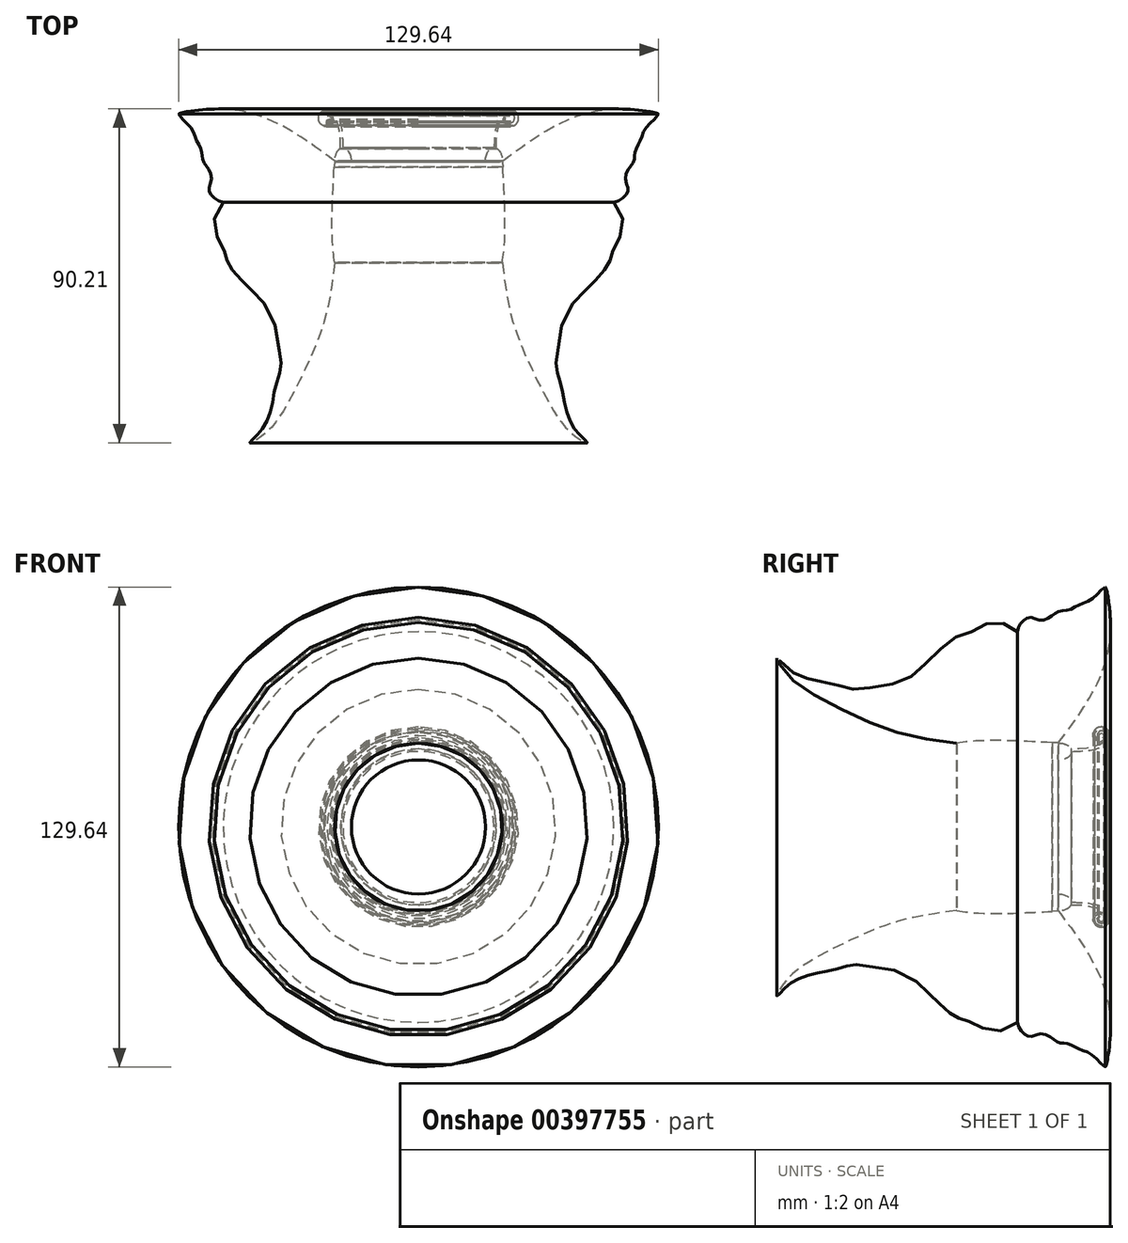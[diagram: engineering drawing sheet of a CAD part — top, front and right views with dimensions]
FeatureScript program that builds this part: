
annotation { "Feature Type Name" : "Feature", "Feature Type Description" : "" }
export const myFeature = defineFeature(function(context is Context, id is Id, definition is map)
    precondition{}
    {
        {
            var Q0;
            Q0=qCreatedBy(makeId("Top.planeOp"),FACE);
            var sketch = newSketch(context, id + "F0", { "sketchPlane" : qUnion([Q0])});
            skEllipticalArc(sketch, "E0", {});
            skEllipticalArc(sketch, "E1", {});
            skFitSpline(sketch, "E2", {"points": [v(2.3, 20.9) * mm, v(2.89, 0) * mm, v(1.74, -9.47) * mm], "startDerivative": vector(2.01, -38.53) * mm, "endDerivative": vector(-3.6, -21.18) * mm});
            skFitSpline(sketch, "E3", {"points": [v(-2.3, 20.9) * mm, v(-3.05, 0) * mm, v(-1.74, -9.47) * mm], "startDerivative": vector(-2.5, -38.54) * mm, "endDerivative": vector(4.14, -21.16) * mm});
            skEllipticalArc(sketch, "E4", {});
            skFitSpline(sketch, "E5", {"points": [v(-2.3, 20.9) * mm, v(0, 20.9) * mm, v(2.3, 20.9) * mm], "startDerivative": vector(4.7, -2.5) * mm, "endDerivative": vector(4.7, 2.5) * mm});
            skFitSpline(sketch, "E6", {"points": [v(-2.4, 19.25) * mm, v(0, 18.83) * mm, v(2.38, 19.24) * mm], "startDerivative": vector(4.9, -2.33) * mm, "endDerivative": vector(4.87, 2.3) * mm});
            skFitSpline(sketch, "E7", {"points": [v(2.3, 20.9) * mm, v(15.85, 30.1) * mm, v(32.92, 34.98) * mm, v(44.41, 33.58) * mm, v(36.58, 33.58) * mm, v(28.57, 33.06) * mm, v(16.1, 28.61) * mm, v(2.38, 19.24) * mm], "startDerivative": vector(81.12, 61.53) * mm, "endDerivative": vector(-77.6, -62.7) * mm});
            skFitSpline(sketch, "E8", {"points": [v(2.38, 19.24) * mm, v(12.47, 14.95) * mm, v(28.81, 10.34) * mm, v(32.38, 9.81) * mm, v(34.78, 10.9) * mm, v(36.24, 13.24) * mm, v(35.51, 15.87) * mm, v(36.39, 18.85) * mm, v(37.78, 20.9) * mm, v(38.21, 23.65) * mm, v(39.54, 26.37) * mm, v(41.1, 29.93) * mm, v(44.41, 33.58) * mm], "startDerivative": vector(70.32, -29.03) * mm, "endDerivative": vector(18.2, 40.24) * mm});
            skFitSpline(sketch, "E9", {"points": [v(2.22, -6.62) * mm, v(4.74, -21.24) * mm, v(9.72, -34.27) * mm, v(16.75, -47.59) * mm, v(22.16, -53.59) * mm, v(25.24, -55.2) * mm, v(22.5, -52.37) * mm, v(20.7, -49.53) * mm, v(19.34, -45.75) * mm, v(18.72, -42.23) * mm, v(17.47, -37.47) * mm, v(16.77, -34.04) * mm, v(17.42, -29.11) * mm, v(19.07, -20.9) * mm, v(22.35, -16.46) * mm, v(27.45, -11.2) * mm, v(31.06, -6.62) * mm, v(32.38, -2.5) * mm, v(34.51, 1.61) * mm, v(34.51, 6.21) * mm, v(32.38, 9.81) * mm], "startDerivative": vector(24.83, -191.18) * mm, "endDerivative": vector(-60.54, 80.48) * mm});
            skEllipse(sketch, "E10", {"center": v(28.24, 24.96) * mm, "majorRadius": 3.27 * mm, "minorRadius": 1.36 * mm, "majorAxis": v(0.84, 0.54)});
            skEllipse(sketch, "E11", {"center": v(28.24, 24.96) * mm, "majorRadius": 1.8 * mm, "minorRadius": 0.84 * mm, "majorAxis": v(0.82, 0.57)});
            skEllipse(sketch, "E12", {"center": v(24.15, 5.65) * mm, "majorRadius": 2.9 * mm, "minorRadius": 1.52 * mm, "majorAxis": v(0.82, -0.57)});
            skEllipse(sketch, "E13", {"center": v(24.15, 5.65) * mm, "majorRadius": 2.05 * mm, "minorRadius": 0.86 * mm, "majorAxis": v(0.76, -0.65)});
            skFitSpline(sketch, "E14", {"points": [v(2.22, -6.62) * mm, v(2.22, -6.56) * mm], "startDerivative": vector(0, 0.06) * mm, "endDerivative": vector(0, 0.06) * mm});
            skLineSegment(sketch, "E15", {"start": v(2.22, -6.56) * mm, "end": v(2.22, -6.55) * mm});
            skArc(sketch, "E16", {"start": v(3.2, 30.63) * mm, "mid": v(6.58, 31.93) * mm, "end": v(4.26, 34.7) * mm});
            skFitSpline(sketch, "E17", {"points": [v(0, 24.44) * mm, v(0.17, 27.52) * mm, v(0.46, 30.02) * mm, v(1.38, 32.67) * mm, v(2.86, 34.16) * mm, v(4.26, 34.7) * mm, v(5.9, 34.15) * mm, v(6.54, 33.17) * mm, v(6.42, 31.5) * mm, v(5.17, 30.4) * mm, v(3.2, 30.63) * mm, v(2.58, 32.37) * mm, v(3.43, 33.46) * mm, v(4.47, 33.63) * mm, v(5.32, 33.33) * mm, v(5.54, 32.83) * mm, v(5.46, 31.98) * mm, v(5, 31.43) * mm, v(4.06, 31.54) * mm, v(3.73, 32.07) * mm, v(4.64, 31.8) * mm, v(5.1, 32.7) * mm, v(4.5, 33.16) * mm, v(3.6, 33) * mm, v(3.02, 32.23) * mm, v(3.46, 31.08) * mm, v(5.02, 30.75) * mm, v(6.02, 31.63) * mm, v(6.13, 33.11) * mm, v(5.5, 33.9) * mm, v(4.27, 34.21) * mm, v(3.05, 33.74) * mm, v(1.87, 32.34) * mm, v(1.14, 29.93) * mm, v(0.72, 27.44) * mm, v(0.67, 24.28) * mm], "startDerivative": vector(3.76, 75.56) * mm, "endDerivative": vector(0.96, -77.04) * mm});
            skFitSpline(sketch, "E18", {"points": [v(2.38, 19.24) * mm, v(6.91, 21.58) * mm, v(16.42, 27.5) * mm, v(28.7, 31.98) * mm, v(36.58, 32.61) * mm, v(43.66, 33.11) * mm, v(36.58, 31.98) * mm, v(28.73, 31.35) * mm, v(16.53, 26.57) * mm, v(7.08, 21.11) * mm, v(2.38, 19.24) * mm]});
            skFitSpline(sketch, "E19", {"points": [v(3.89, 16) * mm, v(8, 13.7) * mm, v(12.47, 11.56) * mm, v(16.7, 10.04) * mm, v(24.01, 8.77) * mm, v(20.07, 8.11) * mm, v(20.15, 5.49) * mm, v(23.1, 2.28) * mm, v(26.97, 1.63) * mm, v(29.1, 2.7) * mm, v(27.05, 0.15) * mm, v(22.12, 1.05) * mm, v(18.5, 4.91) * mm, v(17.52, 7.43) * mm, v(12.47, 9.76) * mm, v(7.59, 12.3) * mm, v(3.89, 16) * mm]});
            skFitSpline(sketch, "E20", {"points": [v(5.46, 9.78) * mm, v(10.98, 6.1) * mm, v(15.51, 2.9) * mm, v(19.7, -3.33) * mm, v(18.04, -7.97) * mm, v(12.47, -7.2) * mm, v(12.47, -2.77) * mm, v(15.68, -3.9) * mm, v(13.83, -5.32) * mm, v(17.46, -5.96) * mm, v(17.35, -3.33) * mm, v(14.6, 0) * mm, v(9.86, 0) * mm, v(8.99, -8.85) * mm, v(10.9, -14.68) * mm, v(14.72, -14.4) * mm, v(16.47, -12.87) * mm, v(12.47, -19.72) * mm, v(12.04, -24.36) * mm, v(10.55, -27.84) * mm, v(8.92, -21.48) * mm, v(8.26, -16.46) * mm, v(7.13, -8.6) * mm, v(6.38, 0) * mm, v(6.08, 2.9) * mm, v(5.85, 7.32) * mm, v(5.46, 9.78) * mm]});
            skPoint(sketch, "E21.6.internal.snap0", {"position": v(27.52, 26.1) * mm});
            skFitSpline(sketch, "E21", {"points": [v(7.6, 19.77) * mm, v(15.95, 23.96) * mm, v(21.25, 26.36) * mm, v(24.34, 28.44) * mm, v(23.14, 24.47) * mm, v(23.41, 22.07) * mm, v(27.52, 21.38) * mm, v(29.13, 21.66) * mm, v(27.1, 19.54) * mm, v(23.04, 18.8) * mm, v(17.7, 18.9) * mm, v(12.3, 19.08) * mm, v(7.6, 19.77) * mm]});
            skFitSpline(sketch, "E22.MirrorCS", {"points": [v(-2.22, -6.62) * mm, v(-2.22, -6.56) * mm], "startDerivative": vector(0, 0.06) * mm, "endDerivative": vector(0, 0.06) * mm});
            skLineSegment(sketch, "E23.MirrorCS", {"start": v(-2.22, -6.56) * mm, "end": v(-2.22, -6.55) * mm});
            skEllipticalArc(sketch, "E24.MirrorCS", {});
            skEllipticalArc(sketch, "E25.MirrorCS", {});
            skFitSpline(sketch, "E26.MirrorCS", {"points": [v(2.3, 20.9) * mm, v(0, 20.9) * mm, v(-2.3, 20.9) * mm], "startDerivative": vector(-4.7, -2.5) * mm, "endDerivative": vector(-4.7, 2.5) * mm});
            skFitSpline(sketch, "E27.MirrorCS", {"points": [v(2.4, 19.25) * mm, v(0, 18.83) * mm, v(-2.38, 19.24) * mm], "startDerivative": vector(-4.9, -2.33) * mm, "endDerivative": vector(-4.87, 2.3) * mm});
            skEllipticalArc(sketch, "E28.MirrorCS", {});
            skLineSegment(sketch, "E29", {"start": v(-20.4, 52.86) * mm, "end": v(-20.4, -60.76) * mm});
            skPoint(sketch, "E30.orphan", {"position": v(0, 43.1) * mm});
            const initialGuessF0  = {"E0": [0, 0.02090463444890858, 0, -1, 0.0035310519394098046, 0.002297039903684678, 1.5707963267948966, 4.71238898038469], "E1": [0, -0.009469367382299913, 0, 1, 0.0035901373358472096, 0.001739675895624183, 1.5707963267948966, 4.71238898038469], "E4": [0.001387894892873516, 0.023718264862181527, 0.3162766123089874, -0.9486670145558718, 0.0018780809074936957, 0.0005518705882354958, 4.293777265012078, 0.42567047345905185], "E24.MirrorCS": [0, 0.02090463444890858, 0, -1, 0.0035310519394098046, 0.002297039903684678, 1.5707963267948966, 4.71238898038469], "E25.MirrorCS": [-0.001387894892873516, 0.023718264862181527, -0.3162766123089874, -0.9486670145558718, 0.0018780809074936957, 0.0005518705882354958, 5.8575148337205345, 1.9894080421675087], "E28.MirrorCS": [0, -0.009469367382299913, 0, 1, 0.0035901373358472096, 0.001739675895624183, 1.5707963267948966, 4.71238898038469]};
            skSetInitialGuess(sketch, initialGuessF0);
            skSolve(sketch);
        }
        {
            var Q0;
            Q0=makeQuery(id+"F0.imprint","IMPRINT",FACE,{"disambiguationData":[TD([[makeQuery(id+"F0.imprint","IMPRINT",EDGE,{"derivedFrom":sQuery(id+"F0.wireOp",EDGE,"E10")}),-1.0]])]});
            var Q1;
            Q1=makeQuery(id+"F0.imprint","IMPRINT",FACE,{"disambiguationData":[TD([[makeQuery(id+"F0.imprint","IMPRINT",EDGE,{"derivedFrom":sQuery(id+"F0.wireOp",EDGE,"E20")}),-1.0]])]});
            var Q2;
            Q2=makeQuery(id+"F0.imprint","IMPRINT",FACE,{"disambiguationData":[TD([[makeQuery(id+"F0.imprint","IMPRINT",EDGE,{"derivedFrom":sQuery(id+"F0.wireOp",EDGE,"E21")}),-1.0]])]});
            var Q3;
            {var subQ0=sQuery(id+"F0.wireOp",EDGE,"E9");Q3=makeQuery(id+"F0.imprint","IMPRINT",FACE,{"disambiguationData":[TD([[makeQuery(id+"F0.imprint","IMPRINT",EDGE,{"derivedFrom":subQ0}),1.0]])]});}
            var Q4;
            {var subQ1=sQuery(id+"F0.wireOp",EDGE,"E7");var subQ5=makeQuery(id+"F0.imprint","INTERSECT",VERTEX,{"derivedFrom":[subQ1,sQuery(id+"F0.wireOp",EDGE,"E8")]});Q4=makeQuery(id+"F0.imprint","IMPRINT",FACE,{"disambiguationData":[TD([[makeQuery(id+"F0.imprint","IMPRINT",EDGE,{"disambiguationData":[TD([[subQ5,-1.0]])],"derivedFrom":subQ1}),-1.0]])]});}
            var Q5;
            {var subQ0=sQuery(id+"F0.wireOp",EDGE,"E28.MirrorCS");Q5=makeQuery(id+"F0.imprint","IMPRINT",FACE,{"disambiguationData":[TD([[makeQuery(id+"F0.imprint","IMPRINT",EDGE,{"derivedFrom":subQ0}),1.0]])]});}
            var Q6;
            Q6=makeQuery(id+"F0.imprint","IMPRINT",FACE,{"disambiguationData":[TD([[makeQuery(id+"F0.imprint","IMPRINT",EDGE,{"derivedFrom":sQuery(id+"F0.wireOp",EDGE,"E10")}),1.0]])]});
            var Q7;
            Q7=makeQuery(id+"F0.imprint","IMPRINT",FACE,{"disambiguationData":[TD([[makeQuery(id+"F0.imprint","IMPRINT",EDGE,{"derivedFrom":sQuery(id+"F0.wireOp",EDGE,"E12")}),1.0]])]});
            var Q8;
            Q8=makeQuery(id+"F0.imprint","IMPRINT",FACE,{"disambiguationData":[TD([[makeQuery(id+"F0.imprint","IMPRINT",EDGE,{"derivedFrom":sQuery(id+"F0.wireOp",EDGE,"E19")}),-1.0]])]});
            var Q9;
            {var subQ0=sQuery(id+"F0.wireOp",EDGE,"E7");var subQ1=makeQuery(id+"F0.imprint","INTERSECT",VERTEX,{"derivedFrom":[subQ0,sQuery(id+"F0.wireOp",EDGE,"E27.MirrorCS")]});Q9=makeQuery(id+"F0.imprint","IMPRINT",FACE,{"disambiguationData":[TD([[makeQuery(id+"F0.imprint","IMPRINT",EDGE,{"disambiguationData":[TD([[subQ1,1.0]])],"derivedFrom":subQ0}),1.0]])]});}
            var Q10;
            {var subQ0=sQuery(id+"F0.wireOp",EDGE,"E17");var subQ1=sQuery(id+"F0.wireOp",EDGE,"E16");var subQ10=makeQuery(id+"F0.imprint","INTERSECT",VERTEX,{"disambiguationData":[OD(0.0)],"derivedFrom":[subQ1,subQ0]});Q10=makeQuery(id+"F0.imprint","IMPRINT",FACE,{"disambiguationData":[TD([[makeQuery(id+"F0.imprint","IMPRINT",EDGE,{"disambiguationData":[TD([[subQ10,-1.0]])],"derivedFrom":subQ1}),1.0]])]});}
            var Q11;
            Q11=makeQuery(id+"F0.imprint","IMPRINT",FACE,{"disambiguationData":[TD([[makeQuery(id+"F0.imprint","IMPRINT",EDGE,{"derivedFrom":sQuery(id+"F0.wireOp",EDGE,"E13")}),1.0]])]});
            var Q12;
            Q12=makeQuery(id+"F0.imprint","IMPRINT",FACE,{"disambiguationData":[TD([[makeQuery(id+"F0.imprint","IMPRINT",EDGE,{"derivedFrom":sQuery(id+"F0.wireOp",EDGE,"E11")}),1.0]])]});
            var Q13;
            {var subQ0=sQuery(id+"F0.wireOp",EDGE,"E17");var subQ1=sQuery(id+"F0.wireOp",EDGE,"E16");var subQ2=makeQuery(id+"F0.imprint","INTERSECT",VERTEX,{"disambiguationData":[OD(0.0)],"derivedFrom":[subQ1,subQ0]});Q13=makeQuery(id+"F0.imprint","IMPRINT",FACE,{"disambiguationData":[TD([[makeQuery(id+"F0.imprint","IMPRINT",EDGE,{"disambiguationData":[TD([[subQ2,-1.0]])],"derivedFrom":subQ1}),-1.0]])]});}
            var Q14;
            {var subQ0=sQuery(id+"F0.wireOp",EDGE,"E17");var subQ1=sQuery(id+"F0.wireOp",EDGE,"E16");var subQ2=makeQuery(id+"F0.imprint","INTERSECT",VERTEX,{"disambiguationData":[OD(2.0)],"derivedFrom":[subQ1,subQ0]});Q14=makeQuery(id+"F0.imprint","IMPRINT",FACE,{"disambiguationData":[TD([[makeQuery(id+"F0.imprint","IMPRINT",EDGE,{"disambiguationData":[TD([[subQ2,-1.0]])],"derivedFrom":subQ1}),1.0]])]});}
            var Q15;
            {var subQ0=sQuery(id+"F0.wireOp",EDGE,"E17");var subQ1=sQuery(id+"F0.wireOp",EDGE,"E16");var subQ2=makeQuery(id+"F0.imprint","INTERSECT",VERTEX,{"disambiguationData":[OD(3.0)],"derivedFrom":[subQ1,subQ0]});Q15=makeQuery(id+"F0.imprint","IMPRINT",FACE,{"disambiguationData":[TD([[makeQuery(id+"F0.imprint","IMPRINT",EDGE,{"disambiguationData":[TD([[subQ2,-1.0]])],"derivedFrom":subQ1}),-1.0]])]});}
            var Q16;
            {var subQ0=sQuery(id+"F0.wireOp",EDGE,"E17");var subQ1=sQuery(id+"F0.wireOp",EDGE,"E16");var subQ2=makeQuery(id+"F0.imprint","INTERSECT",VERTEX,{"disambiguationData":[OD(4.0)],"derivedFrom":[subQ1,subQ0]});Q16=makeQuery(id+"F0.imprint","IMPRINT",FACE,{"disambiguationData":[TD([[makeQuery(id+"F0.imprint","IMPRINT",EDGE,{"disambiguationData":[TD([[subQ2,-1.0]])],"derivedFrom":subQ1}),1.0]])]});}
            var Q17;
            {var subQ0=sQuery(id+"F0.wireOp",EDGE,"E17");var subQ1=sQuery(id+"F0.wireOp",EDGE,"E16");var subQ2=makeQuery(id+"F0.imprint","INTERSECT",VERTEX,{"disambiguationData":[OD(5.0)],"derivedFrom":[subQ1,subQ0]});Q17=makeQuery(id+"F0.imprint","IMPRINT",FACE,{"disambiguationData":[TD([[makeQuery(id+"F0.imprint","IMPRINT",EDGE,{"disambiguationData":[TD([[subQ2,-1.0]])],"derivedFrom":subQ1}),-1.0]])]});}
            var Q18;
            {var subQ0=sQuery(id+"F0.wireOp",EDGE,"E17");var subQ1=sQuery(id+"F0.wireOp",EDGE,"E16");var subQ2=makeQuery(id+"F0.imprint","INTERSECT",VERTEX,{"disambiguationData":[OD(1.0)],"derivedFrom":[subQ1,subQ0]});Q18=makeQuery(id+"F0.imprint","IMPRINT",FACE,{"disambiguationData":[TD([[makeQuery(id+"F0.imprint","IMPRINT",EDGE,{"disambiguationData":[TD([[subQ2,1.0]])],"derivedFrom":subQ1}),1.0]])]});}
            var Q19;
            {var subQ0=sQuery(id+"F0.wireOp",EDGE,"E4");Q19=makeQuery(id+"F0.imprint","IMPRINT",FACE,{"disambiguationData":[TD([[makeQuery(id+"F0.imprint","IMPRINT",EDGE,{"derivedFrom":subQ0}),1.0]])]});}
            var Q20;
            {var subQ0=sQuery(id+"F0.wireOp",EDGE,"E25.MirrorCS");Q20=makeQuery(id+"F0.imprint","IMPRINT",FACE,{"disambiguationData":[TD([[makeQuery(id+"F0.imprint","IMPRINT",EDGE,{"derivedFrom":subQ0}),1.0]])]});}
            var Q21;
            {var subQ5=sQuery(id+"F0.wireOp",EDGE,"E4");Q21=makeQuery(id+"F0.imprint","IMPRINT",FACE,{"disambiguationData":[TD([[makeQuery(id+"F0.imprint","IMPRINT",EDGE,{"derivedFrom":subQ5}),-1.0]])]});}
            var Q22;
            {var subQ0=sQuery(id+"F0.wireOp",EDGE,"E26.MirrorCS");Q22=makeQuery(id+"F0.imprint","IMPRINT",FACE,{"disambiguationData":[TD([[makeQuery(id+"F0.imprint","IMPRINT",EDGE,{"derivedFrom":subQ0}),1.0]])]});}
            var Q23;
            {var subQ0=sQuery(id+"F0.wireOp",EDGE,"E27.MirrorCS");var subQ1=sQuery(id+"F0.wireOp",EDGE,"E2");var subQ2=makeQuery(id+"F0.imprint","INTERSECT",VERTEX,{"derivedFrom":[subQ1,subQ0]});Q23=makeQuery(id+"F0.imprint","IMPRINT",FACE,{"disambiguationData":[TD([[makeQuery(id+"F0.imprint","IMPRINT",EDGE,{"disambiguationData":[TD([[subQ2,-1.0]])],"derivedFrom":subQ1}),-1.0]])]});}
            var Q24;
            {var subQ0=sQuery(id+"F0.wireOp",EDGE,"E27.MirrorCS");var subQ1=sQuery(id+"F0.wireOp",EDGE,"E7");var subQ2=makeQuery(id+"F0.imprint","INTERSECT",VERTEX,{"derivedFrom":[subQ1,subQ0]});Q24=makeQuery(id+"F0.imprint","IMPRINT",FACE,{"disambiguationData":[TD([[makeQuery(id+"F0.imprint","IMPRINT",EDGE,{"disambiguationData":[TD([[subQ2,1.0]])],"derivedFrom":subQ1}),-1.0]])]});}
            var Q25;
            {var subQ0=sQuery(id+"F0.wireOp",EDGE,"E18");var subQ1=sQuery(id+"F0.wireOp",EDGE,"E2");var subQ3=makeQuery(id+"F0.imprint","INTERSECT",VERTEX,{"derivedFrom":[subQ1,subQ0]});Q25=makeQuery(id+"F0.imprint","IMPRINT",FACE,{"disambiguationData":[TD([[makeQuery(id+"F0.imprint","IMPRINT",EDGE,{"disambiguationData":[TD([[subQ3,-1.0]])],"derivedFrom":subQ1}),-1.0]])]});}
            var Q26;
            {var subQ0=sQuery(id+"F0.wireOp",EDGE,"E18");var subQ1=sQuery(id+"F0.wireOp",EDGE,"E8");var subQ3=makeQuery(id+"F0.imprint","INTERSECT",VERTEX,{"derivedFrom":[subQ1,subQ0]});Q26=makeQuery(id+"F0.imprint","IMPRINT",FACE,{"disambiguationData":[TD([[makeQuery(id+"F0.imprint","IMPRINT",EDGE,{"disambiguationData":[TD([[subQ3,1.0]])],"derivedFrom":subQ1}),-1.0]])]});}
            var Q27;
            {var subQ0=sQuery(id+"F0.wireOp",EDGE,"E18");var subQ2=sQuery(id+"F0.wireOp",EDGE,"E2");var subQ4=makeQuery(id+"F0.imprint","INTERSECT",VERTEX,{"derivedFrom":[subQ2,subQ0]});Q27=makeQuery(id+"F0.imprint","IMPRINT",FACE,{"disambiguationData":[TD([[makeQuery(id+"F0.imprint","IMPRINT",EDGE,{"disambiguationData":[TD([[subQ4,-1.0]])],"derivedFrom":subQ0}),-1.0]])]});}
            var Q28;
            {var subQ0=sQuery(id+"F0.wireOp",EDGE,"E27.MirrorCS");var subQ1=sQuery(id+"F0.wireOp",EDGE,"E2");var subQ2=makeQuery(id+"F0.imprint","INTERSECT",VERTEX,{"derivedFrom":[subQ1,subQ0]});Q28=makeQuery(id+"F0.imprint","IMPRINT",FACE,{"disambiguationData":[TD([[makeQuery(id+"F0.imprint","IMPRINT",EDGE,{"disambiguationData":[TD([[subQ2,-1.0]])],"derivedFrom":subQ1}),1.0]])]});}
            var Q29;
            Q29=sQuery(id+"F0.wireOp",EDGE,"E29");
            revolve(context, id + "F1", {"entities" : qUnion([Q0, Q1, Q2, Q3, Q4, Q5, Q6, Q7, Q8, Q9, Q10, Q11, Q12, Q13, Q14, Q15, Q16, Q17, Q18, Q19, Q20, Q21, Q22, Q23, Q24, Q25, Q26, Q27, Q28]), "axis" : qUnion([Q29]), "revolveType" : RevolveType.FULL});
        }
    });
